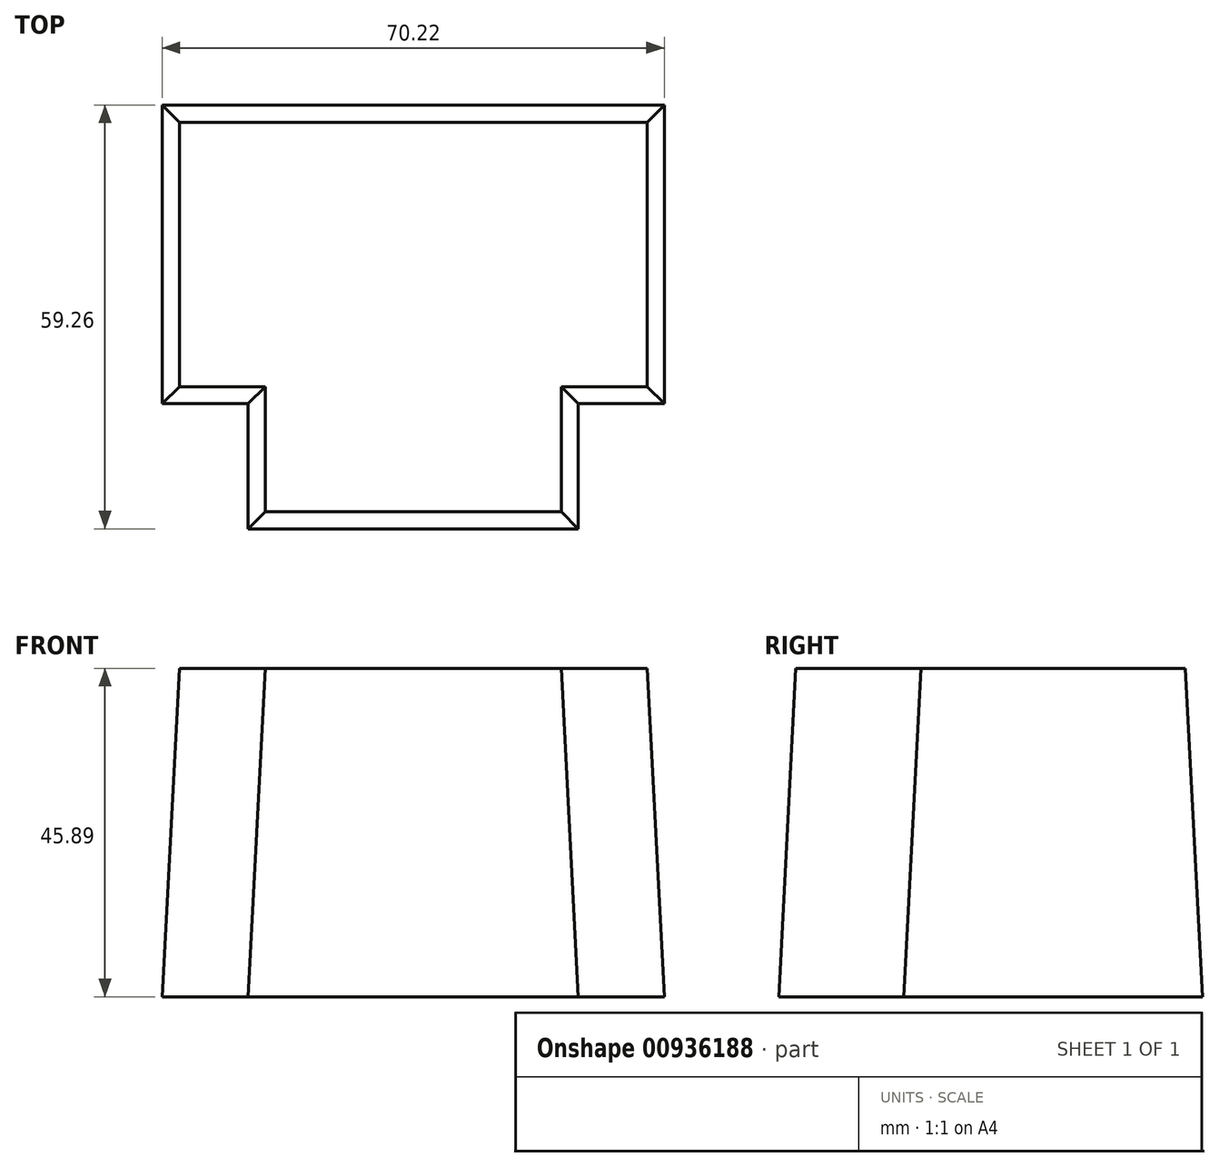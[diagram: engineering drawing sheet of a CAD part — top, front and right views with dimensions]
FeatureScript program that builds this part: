
annotation { "Feature Type Name" : "Feature", "Feature Type Description" : "" }
export const myFeature = defineFeature(function(context is Context, id is Id, definition is map)
    precondition{}
    {
        {
            var Q0;
            Q0=qCreatedBy(makeId("Top.planeOp"),FACE);
            var sketch = newSketch(context, id + "F0", { "sketchPlane" : qUnion([Q0])});
            skLineSegment(sketch, "E0.bottom", {"start": v(35.1, 83.06) * mm, "end": v(-35.1, 83.06) * mm});
            skLineSegment(sketch, "E0.top", {"start": v(35.1, 41.3) * mm, "end": v(-35.1, 41.3) * mm});
            skLineSegment(sketch, "E0.left", {"start": v(35.1, 83.06) * mm, "end": v(35.1, 41.3) * mm});
            skLineSegment(sketch, "E0.right", {"start": v(-35.1, 83.06) * mm, "end": v(-35.1, 41.3) * mm});
            skPoint(sketch, "E0.middle", {"position": v(0, 62.17) * mm});
            skLineSegment(sketch, "E1.bottom", {"start": v(23.1, 23.8) * mm, "end": v(-23.1, 23.8) * mm});
            skLineSegment(sketch, "E1.top", {"start": v(23.1, 58.78) * mm, "end": v(-23.1, 58.78) * mm});
            skLineSegment(sketch, "E1.left", {"start": v(23.1, 23.8) * mm, "end": v(23.1, 58.78) * mm});
            skLineSegment(sketch, "E1.right", {"start": v(-23.1, 23.8) * mm, "end": v(-23.1, 58.78) * mm});
            skPoint(sketch, "E1.middle", {"position": v(0, 41.3) * mm});
            skSolve(sketch);
        }
        {
            var Q0;
            Q0 = qSketchRegion(id + "F0", true);
            extrude(context, id + "F1", {"entities" : qUnion([Q0]), "depth" : 45.9 * mm, "offsetDistance" : 25.4 * mm, "hasDraft" : true, "draftAngle" : 3 * degree, "draftPullDirection" : true});
        }
    });
